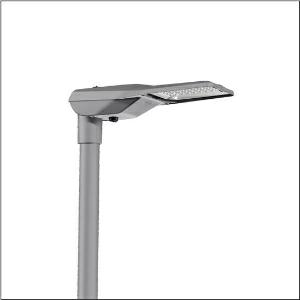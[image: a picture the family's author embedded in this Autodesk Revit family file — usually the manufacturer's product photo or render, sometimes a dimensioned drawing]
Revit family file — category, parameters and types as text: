
# Revit family: streetlight_sl_21_mini___p0_8a_5xe2u33t08jb_ddfb
name_source: partatom
category: Lighting Fixtures
units: mm (PartAtom-declared; Revit-internal decimal feet)

## family parameters
Cut with Voids When Loaded = No
Host = Face
Light Source = No
Part Type = Normal
Room Calculation Point = No
Round Connector Dimension = Use Diameter
Shared = No

## types (1)
- --- (1 x LED, 13050 lm, 88.6 W, 3000K)
    Apparent Load = 89 VA
    CIE Flux Codes = 36 69 97 100 100
    Color Rendering = 70
    Color Temperature = 3000K
    Default Elevation = 1800 mm
    Description = Streetlight SL 21 mini, mast luminaire, primary light control with lens, of PMMA, primary optical cover: cover, of toughened safety glass, transparent, light distribution: P0.8a, light emission: direct distribution, primary light characteristic: asymmetric, installation type: post-top, side-entry, LED, High Power LED, rated luminous flux: 13.050lm, luminous efficacy: 147lm/W, light colour: 730, colour temperature: 3000K, control gear: D4i, control: pre-setting: logarithmic dimming characteristic, flexible luminous flux parameterisation, time-dependent luminous flux control, constant luminous flux control, overheat protection, mains connection: 220..240V, AC, 50/60Hz, start of lifetime: 89W, end of service life: 92W, reduction: 41W, luminaire housing, of diecast aluminium, powder-coated, Siteco® metallic grey (DB 702S), corrosivity category C5 high according to DIN EN ISO 12944, multi-level sealing system, sealing non-destructively replaceable, inclination adjustable: 0°, 5°, 10°, 15°, please order mast flange separately, length: 628mm, width: 235mm, height: 110mm, mast flange for spigot size: 42mm (side-entry): 5XC10008XM4, 60/48mm (side-entry/post-top): 5XC10108XM2, 76/60mm (side-entry/post-top): 5XC10108XM1, mounting height: 4..8m, Smart Interface below and above, protection rating (complete): IP66, insulation class (complete): insulation class II (safety insulation), certification: CE, ENEC, ENEC+, VDE, impact resistance: IK10, permissible operating ambient temperature for outdoor applications: -40..+50°C, standard-compliant lighting for roads and squares, packaging unit: 1 piece

Light Distribution: P0.8a
    Height = 110 mm
    Lamp = 1 x LED
    Lamp Light Flux = 13050 lm
    Lamp Power = 88.6 W
    Lamp count = 1
    Length = 625 mm
    Luminous efficacy = 147 lm/W
    Manufacturer = Siteco
    ModVariant = No
    Model = 5XE2U33T08JB
    Number of Poles = 1
    OnlyDefault = Yes
    Power Factor = 1
    Product Name = Streetlight SL 21 mini | P0.8a
    Product group = mast luminaire | pylon top
    ProductGroupID = 6100
    Protection Class = Protection class II
    Protection Degree = IP 66
    RLX_Detail_Level = 1
    RLX_Emergency_Light_Flux = 0 lm
    RLX_Emergency_Type = 0
    RLX_Emergency_Type_DB = No
    RlxData = <blob elided: 26249 chars, md5=c9f8fde7>
    Socket = socket
    Standby Power = 0 W
    System Light Flux = 13050 lm
    System Power = 89 W
    Type Comments = factory setting: luminous flux: 100 % | dim-lin: 254 | 915 mA
    Type Image = l_1003514.jpg
    URL = http://relux.com
    VarID = @adj_032741
    Voltage = 0 V
    Weight = 0.00 kg
    Width = 234 mm

## geometry (parser evidence)
native form markers: Blend x4, Sweep x10
no freeform markers — native parametric forms only
